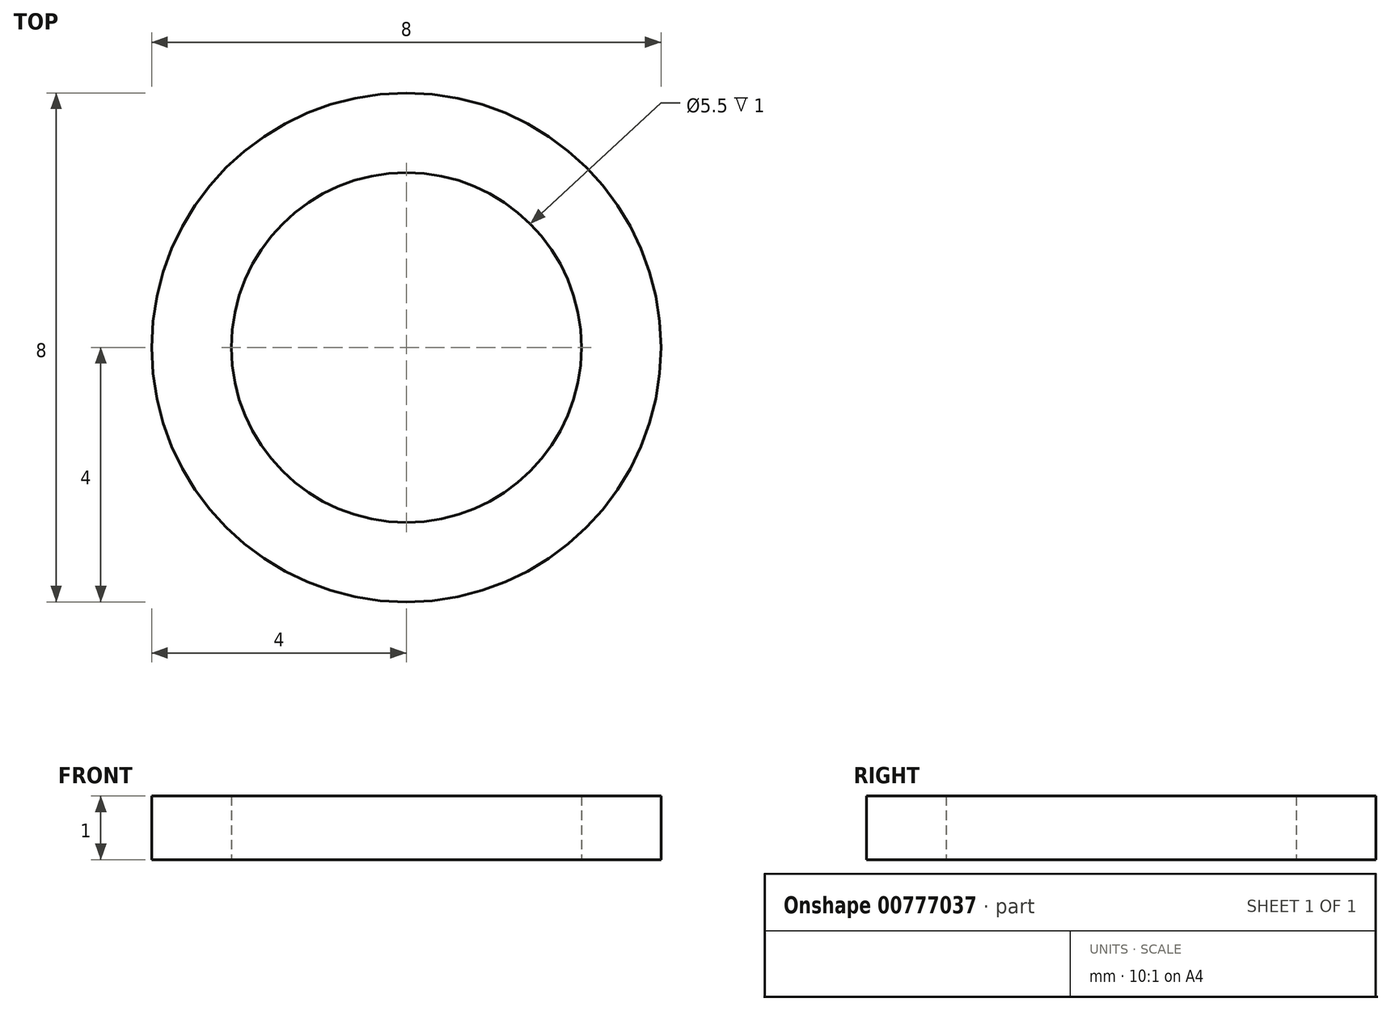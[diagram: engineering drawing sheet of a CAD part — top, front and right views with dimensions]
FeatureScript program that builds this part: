
annotation { "Feature Type Name" : "Feature", "Feature Type Description" : "" }
export const myFeature = defineFeature(function(context is Context, id is Id, definition is map)
    precondition{}
    {
        {
            var Q0;
            Q0=qCreatedBy(makeId("Top.planeOp"),FACE);
            var sketch = newSketch(context, id + "F0", { "sketchPlane" : qUnion([Q0])});
            skCircle(sketch, "E0", {"center": v(0, 0) * mm, "radius": 2.75 * mm});
            skCircle(sketch, "E1", {"center": v(0, 0) * mm, "radius": 4 * mm});
            skSolve(sketch);
        }
        {
            var Q0;
            Q0=qSketchRegion(id+"F0",true);
            extrude(context, id + "F1", {"entities" : qUnion([Q0]), "depth" : 1 * mm, "offsetDistance" : 25 * mm});
        }
    });
